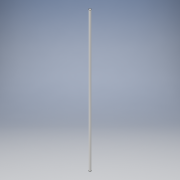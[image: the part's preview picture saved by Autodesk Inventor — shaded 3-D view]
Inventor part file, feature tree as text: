
AUTODESK INVENTOR PART (.ipt)
format: ipt  version: 2019 (Build 230136000, 136)  size: 89,600 bytes
history: native  units: mm
features: extrude x1, sketch x1
ambient origin geometry x8: Origin, YZ Plane, XZ Plane, XY Plane, X Axis, Y Axis, Z Axis, Center Point
bodies: Solid1 (feature_tree)
feature tree (2):
  extrude  "Extrusion1"  Depth=1000.0mm TaperAngle=0.0deg
  sketch  "Sketch1"  dims[d0=15.0mm d1=1000.0mm d2=0.0mm]
